# Revit family: LEGRAND_PRISES_NON_VERROUILLEES_SAILLIES_IP44_40
name_source: partatom
category: Installations électriques
revit_build: Autodesk Revit 2018 (Build: 20170223_1515(x64)
units: mm (PartAtom-declared; Revit-internal decimal feet)

## family parameters
Conserver l'orientation des annotations = Non
Cote de connecteur circulaire = Utiliser le diamètre
Couper avec des vides une fois chargée = Non
Hôte = Face
Partagée = Non
Point de calcul de pièce = Non
Type d'élément = Normal

## types (3) — shared parameters
Conditions Générale d'Utilisation = https://export.legrand.com
Couleur caractéristique = blanc
Description = Prise au standard international pour montage encastré ou saillie avec accessoire permet la connexion d'appareils de puissance
Dia bouchon = 48 mm
Elévation par défaut = 1000 mm  [stored 3.28084 ft]
Fabricant = Legrand
Intensité A = 16 A
RAY BOUCHON = 24 mm
Ray = 24 mm
Standard CEI ou NFC = CEI
Température maximale d'installation = 40°C
Température maximum d'utilisation = 100°C
Température minimum d'installation = -20°C
Température minimum d'utilisation = -50°C
Tension V = 40 50 V  50/60 Hz  blanc
classe de protection IP = IP44
entraxe de fixation horizontal mm = 52 mm
entraxe de fixation vertical mm = 60 mm
h1 = 64 mm
hauteur mm = 106 mm  [stored 0.347769 ft]
installation Encastrée E ou Saillie S = encastré et saillie
largeur mm = 74 mm  [stored 0.242782 ft]
matériau du boitier = plastique
profondeur d'encastrement mm = 58 mm  [stored 0.190289 ft]
résistance aux chocs IK = 09
sans halogène = Oui
type de raccordement = bornes à vis

## per-type parameters (varying)
| type | Modèle | Nombre de pôles | Position de la Terre h | profondeur mm |
| Socle tableau Hypra   IP44   TBT 16 A   40/50V   2P   plast saillie boitier simple | 052403 | 2 | 12 | 105 mm  [stored 0.344488 ft] |
| Socle tableau Hypra   IP44   TBT 16 A   40/50V   3P   plast saillie boitier simple | 052404 | 3 | 12 | 97 mm |
| Socle tableau Hypra   IP44   TBT 16 A   20/50 V continu   2P   plast saillie boitier simple | 052405 | 2 | 10 | 105 mm  [stored 0.344488 ft] |

note: [stored X ft] marks values corroborated as IEEE doubles in the binary element streams (Revit-internal decimal feet)
